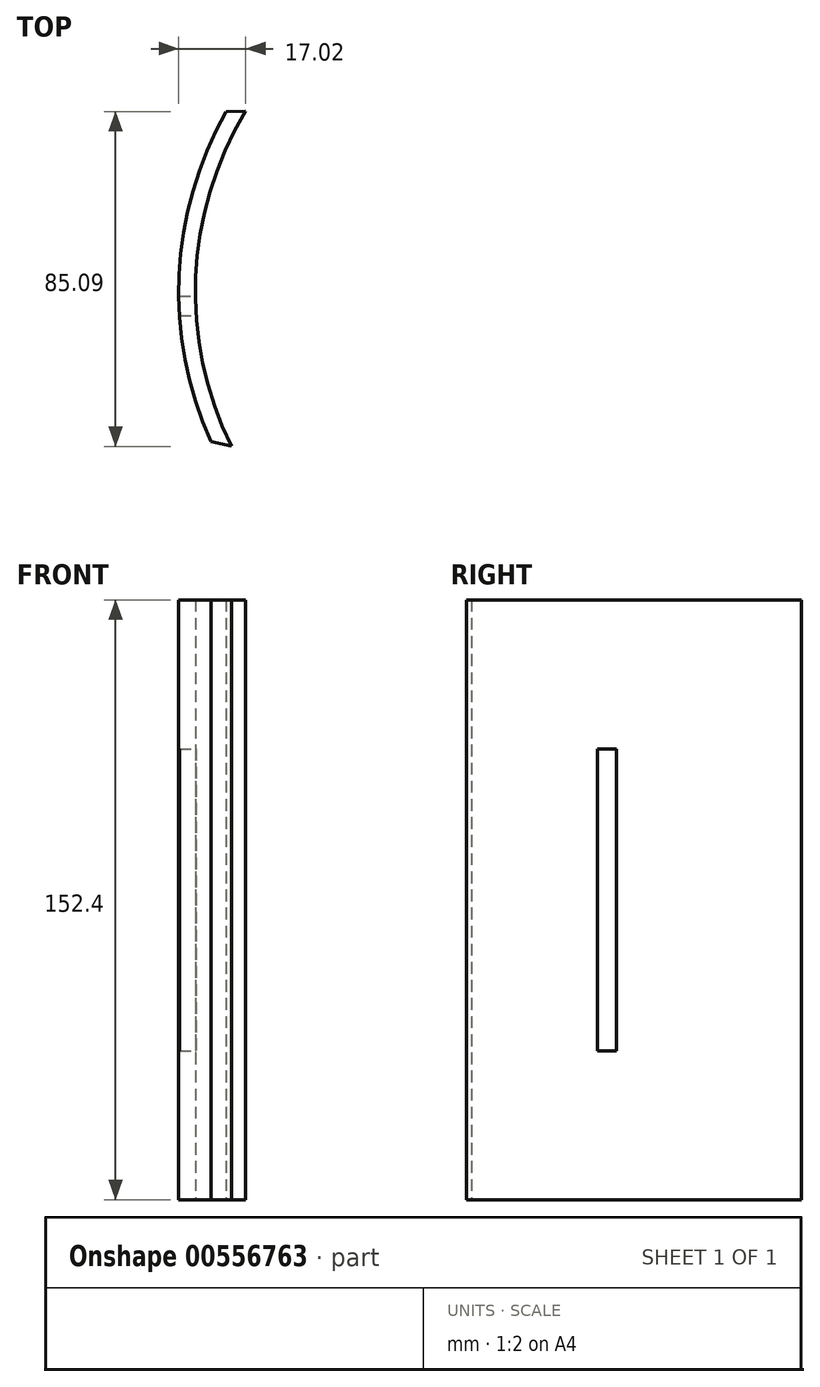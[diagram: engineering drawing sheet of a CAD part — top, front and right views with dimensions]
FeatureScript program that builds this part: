
annotation { "Feature Type Name" : "Feature", "Feature Type Description" : "" }
export const myFeature = defineFeature(function(context is Context, id is Id, definition is map)
    precondition{}
    {
        {
            var Q0;
            Q0=qCreatedBy(makeId("Top.planeOp"),FACE);
            var sketch = newSketch(context, id + "F0", { "sketchPlane" : qUnion([Q0])});
            skArc(sketch, "E0", {"start": v(-19.17, -4.94) * mm, "mid": v(-31.16, -46.38) * mm, "end": v(-23.1, -88.76) * mm});
            skArc(sketch, "E1.0", {"start": v(-14.24, -4.89) * mm, "mid": v(-26.95, -46.97) * mm, "end": v(-17.84, -89.98) * mm});
            skLineSegment(sketch, "E2", {"start": v(-19.17, -4.94) * mm, "end": v(-14.24, -4.89) * mm});
            skLineSegment(sketch, "E3", {"start": v(-23.1, -88.76) * mm, "end": v(-17.84, -89.98) * mm});
            skSolve(sketch);
        }
        {
            var Q0;
            Q0=makeQuery(id+"F0.imprint","IMPRINT",FACE,{"disambiguationData":[TD([[makeQuery(id+"F0.imprint","IMPRINT",EDGE,{"derivedFrom":sQuery(id+"F0.wireOp",EDGE,"E0")}),1.0]])]});
            extrude(context, id + "F1", {"entities" : qUnion([Q0]), "endBound" : BoundingType.SYMMETRIC, "depth" : 152.4 * mm, "offsetDistance" : 25.4 * mm});
        }
        {
            var Q0;
            Q0=qCreatedBy(makeId("Right.planeOp"),FACE);
            var sketch = newSketch(context, id + "F2", { "sketchPlane" : qUnion([Q0])});
            skLineSegment(sketch, "E4.bottom", {"start": v(-51.88, 38.35) * mm, "end": v(-56.79, 38.35) * mm});
            skLineSegment(sketch, "E4.top", {"start": v(-51.88, -38.35) * mm, "end": v(-56.79, -38.35) * mm});
            skLineSegment(sketch, "E4.left", {"start": v(-51.88, 38.35) * mm, "end": v(-51.88, -38.35) * mm});
            skLineSegment(sketch, "E4.right", {"start": v(-56.79, 38.35) * mm, "end": v(-56.79, -38.35) * mm});
            skPoint(sketch, "E4.middle", {"position": v(-54.33, 0) * mm});
            skSolve(sketch);
        }
        {
            var Q0;
            Q0=makeQuery(id+"F2.imprint","IMPRINT",FACE,{"disambiguationData":[TD([[makeQuery(id+"F2.imprint","IMPRINT",EDGE,{"derivedFrom":sQuery(id+"F2.wireOp",EDGE,"E4.bottom")}),1.0]])]});
            extrude(context, id + "F3", {"entities" : qUnion([Q0]), "operationType" : NewBodyOperationType.REMOVE, "oppositeDirection" : true, "depth" : 50.8 * mm, "offsetDistance" : 25.4 * mm});
        }
    });
